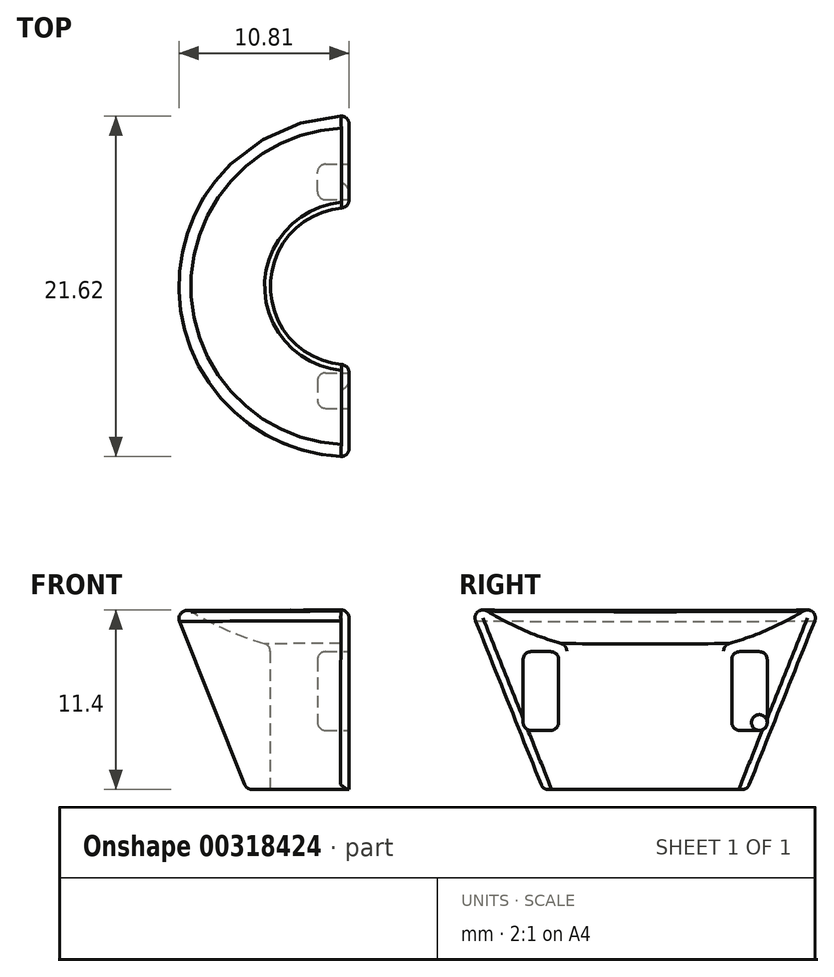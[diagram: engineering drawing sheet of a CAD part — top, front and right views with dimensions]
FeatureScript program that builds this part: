
annotation { "Feature Type Name" : "Feature", "Feature Type Description" : "" }
export const myFeature = defineFeature(function(context is Context, id is Id, definition is map)
    precondition{}
    {
        {
            var Q0;
            Q0=qCreatedBy(makeId("Top.planeOp"),FACE);
            var sketch = newSketch(context, id + "F0", { "sketchPlane" : qUnion([Q0])});
            skCircle(sketch, "E0", {"center": v(0, 0) * mm, "radius": 6.5 * mm});
            skSolve(sketch);
        }
        {
            var Q0;
            Q0=qCreatedBy(makeId("Top.planeOp"),FACE);
            cPlane(context, id + "F1", {"entities" : qUnion([Q0]), "cplaneType" : CPlaneType.OFFSET, "offset" : 15 * mm, "width" : 150 * mm, "height" : 150 * mm});
        }
        {
            var Q0;
            Q0=qCreatedBy(id+"F1.planeOp",FACE);
            var sketch = newSketch(context, id + "F2", { "sketchPlane" : qUnion([Q0])});
            skCircle(sketch, "E1", {"center": v(0, 0) * mm, "radius": 12.5 * mm});
            skSolve(sketch);
        }
        {
            var Q0;
            Q0=makeQuery(id+"F0.imprint","IMPRINT",FACE,{"disambiguationData":[TD([[makeQuery(id+"F0.imprint","IMPRINT",EDGE,{"derivedFrom":sQuery(id+"F0.wireOp",EDGE,"E0")}),1.0]])]});
            var Q1;
            Q1=makeQuery(id+"F2.imprint","IMPRINT",FACE,{"disambiguationData":[TD([[makeQuery(id+"F2.imprint","IMPRINT",EDGE,{"derivedFrom":sQuery(id+"F2.wireOp",EDGE,"E1")}),1.0]])]});
            loft(context, id + "F3", {"sheetProfilesArray" : [{ "sheetProfileEntities" : qUnion([Q0]) }, { "sheetProfileEntities" : qUnion([Q1]) }]});
        }
        {
            var Q0;
            Q0=makeQuery(id+"F3.opLoft","CAP_FACE",FACE,{"disambiguationData":[OSD([makeQuery(id+"F0.imprint","IMPRINT",FACE,{"disambiguationData":[TD([[makeQuery(id+"F0.imprint","IMPRINT",EDGE,{"derivedFrom":sQuery(id+"F0.wireOp",EDGE,"E0")}),1.0]])]})])],"isStart":true});
            var sketch = newSketch(context, id + "F4", { "sketchPlane" : qUnion([Q0])});
            skCircle(sketch, "E2", {"center": v(0, 0) * mm, "radius": 5 * mm});
            skSolve(sketch);
        }
        {
            var Q0;
            Q0=makeQuery(id+"F4.imprint","IMPRINT",FACE,{"disambiguationData":[TD([[makeQuery(id+"F4.imprint","IMPRINT",EDGE,{"derivedFrom":sQuery(id+"F4.wireOp",EDGE,"E2")}),1.0]])]});
            extrude(context, id + "F5", {"entities" : qUnion([Q0]), "operationType" : NewBodyOperationType.REMOVE, "oppositeDirection" : true, "depth" : 10 * mm});
        }
        {
            var Q0;
            Q0=qCreatedBy(makeId("Front.planeOp"),FACE);
            var sketch = newSketch(context, id + "F6", { "sketchPlane" : qUnion([Q0])});
            skArc(sketch, "E3", {"start": v(0.03, 47.5) * mm, "mid": v(-19.5, 28.09) * mm, "end": v(-0.14, 8.5) * mm});
            skLineSegment(sketch, "E4", {"start": v(-0.14, 8.5) * mm, "end": v(0.03, 47.5) * mm});
            skSolve(sketch);
        }
        {
            var Q0;
            Q0=makeQuery(id+"F6.imprint","IMPRINT",FACE,{"disambiguationData":[TD([[makeQuery(id+"F6.imprint","IMPRINT",EDGE,{"derivedFrom":sQuery(id+"F6.wireOp",EDGE,"E3")}),1.0]])]});
            var Q1;
            Q1=sQuery(id+"F6.wireOp",EDGE,"E4");
            revolve(context, id + "F7", {"operationType" : NewBodyOperationType.REMOVE, "entities" : qUnion([Q0]), "axis" : qUnion([Q1]), "revolveType" : RevolveType.FULL});
        }
        {
            var Q0;
            Q0=qCreatedBy(makeId("Front.planeOp"),FACE);
            var sketch = newSketch(context, id + "F8", { "sketchPlane" : qUnion([Q0])});
            skLineSegment(sketch, "E5.bottom", {"start": v(0, 0) * mm, "end": v(15, 0) * mm});
            skLineSegment(sketch, "E5.top", {"start": v(0, 15) * mm, "end": v(15, 15) * mm});
            skLineSegment(sketch, "E5.left", {"start": v(0, 0) * mm, "end": v(0, 15) * mm});
            skLineSegment(sketch, "E5.right", {"start": v(15, 0) * mm, "end": v(15, 15) * mm});
            skSolve(sketch);
        }
        {
            var Q0;
            Q0=makeQuery(id+"F8.imprint","IMPRINT",FACE,{"disambiguationData":[TD([[makeQuery(id+"F8.imprint","IMPRINT",EDGE,{"derivedFrom":sQuery(id+"F8.wireOp",EDGE,"E5.bottom")}),1.0]])]});
            extrude(context, id + "F9", {"entities" : qUnion([Q0]), "operationType" : NewBodyOperationType.REMOVE, "depth" : 25 * mm, "hasSecondDirection" : true, "secondDirectionOppositeDirection" : true, "secondDirectionDepth" : 25 * mm});
        }
        {
            var Q0;
            Q0=makeQuery(id+"FPjt2AgAj65mRvz_1.boolean.opBoolean","SPLIT",FACE,{"disambiguationData":[OD(0.0)],"derivedFrom":makeQuery(id+"F9.boolean.opBoolean","COPY",FACE,{"derivedFrom":makeQuery(id+"F9.opExtrude","SWEPT_FACE",FACE,{"disambiguationData":[OSD([sQuery(id+"F8.wireOp",EDGE,"E5.left")])]})})});
            var sketch = newSketch(context, id + "F10", { "sketchPlane" : qUnion([Q0])});
            skLineSegment(sketch, "E6.bottom", {"start": v(-6, 8.75) * mm, "end": v(-7.25, 8.75) * mm});
            skLineSegment(sketch, "E6.top", {"start": v(-6, 3.75) * mm, "end": v(-7.25, 3.75) * mm});
            skLineSegment(sketch, "E6.left", {"start": v(-5.5, 8.25) * mm, "end": v(-5.5, 4.25) * mm});
            skLineSegment(sketch, "E6.right", {"start": v(-7.75, 8.25) * mm, "end": v(-7.75, 4.25) * mm});
            skPoint(sketch, "E7.visualSharp", {"position": v(-7.75, 8.75) * mm});
            skArc(sketch, "E7.filletArc", {"start": v(-7.25, 8.75) * mm, "mid": v(-7.6, 8.6) * mm, "end": v(-7.75, 8.25) * mm});
            skPoint(sketch, "E8.visualSharp", {"position": v(-5.5, 8.75) * mm});
            skArc(sketch, "E8.filletArc", {"start": v(-5.5, 8.25) * mm, "mid": v(-5.65, 8.6) * mm, "end": v(-6, 8.75) * mm});
            skPoint(sketch, "E9.visualSharp", {"position": v(-5.5, 3.75) * mm});
            skArc(sketch, "E9.filletArc", {"start": v(-6, 3.75) * mm, "mid": v(-5.65, 3.9) * mm, "end": v(-5.5, 4.25) * mm});
            skPoint(sketch, "E10.visualSharp", {"position": v(-7.75, 3.75) * mm});
            skArc(sketch, "E10.filletArc", {"start": v(-7.75, 4.25) * mm, "mid": v(-7.6, 3.9) * mm, "end": v(-7.25, 3.75) * mm});
            skLineSegment(sketch, "E11.MirrorCS", {"start": v(5.5, 8.25) * mm, "end": v(5.5, 4.25) * mm});
            skArc(sketch, "E12.MirrorCS", {"start": v(5.5, 8.25) * mm, "mid": v(5.65, 8.6) * mm, "end": v(6, 8.75) * mm});
            skLineSegment(sketch, "E13.MirrorCS", {"start": v(6, 8.75) * mm, "end": v(7.25, 8.75) * mm});
            skArc(sketch, "E14.MirrorCS", {"start": v(7.25, 8.75) * mm, "mid": v(7.6, 8.6) * mm, "end": v(7.75, 8.25) * mm});
            skLineSegment(sketch, "E15.MirrorCS", {"start": v(7.75, 8.25) * mm, "end": v(7.75, 4.25) * mm});
            skPoint(sketch, "E16.MirrorP", {"position": v(7.75, 3.75) * mm});
            skArc(sketch, "E17.MirrorCS", {"start": v(7.75, 4.25) * mm, "mid": v(7.6, 3.9) * mm, "end": v(7.25, 3.75) * mm});
            skLineSegment(sketch, "E18.MirrorCS", {"start": v(6, 3.75) * mm, "end": v(7.25, 3.75) * mm});
            skArc(sketch, "E19.MirrorCS", {"start": v(6, 3.75) * mm, "mid": v(5.65, 3.9) * mm, "end": v(5.5, 4.25) * mm});
            skSolve(sketch);
        }
        {
            var Q0;
            Q0=makeQuery(id+"F10.imprint","IMPRINT",FACE,{"disambiguationData":[TD([[makeQuery(id+"F10.imprint","IMPRINT",EDGE,{"derivedFrom":sQuery(id+"F10.wireOp",EDGE,"E6.bottom")}),1.0]])]});
            var Q1;
            Q1=makeQuery(id+"F10.imprint","IMPRINT",FACE,{"disambiguationData":[TD([[makeQuery(id+"F10.imprint","IMPRINT",EDGE,{"derivedFrom":sQuery(id+"F10.wireOp",EDGE,"E11.MirrorCS")}),1.0]])]});
            extrude(context, id + "F11", {"entities" : qUnion([Q0, Q1]), "operationType" : NewBodyOperationType.REMOVE, "oppositeDirection" : true, "depth" : 2 * mm});
        }
        {
            var Q0;
            Q0=makeQuery(id+"F7.boolean.opBoolean","INTERSECT",EDGE,{"derivedFrom":[makeQuery(id+"F3.opLoft","SWEPT_FACE",FACE,{"disambiguationData":[OSD([sQuery(id+"F0.wireOp",EDGE,"E0"),sQuery(id+"F2.wireOp",EDGE,"E1")])]}),makeQuery(id+"F7.opRevolve","SWEPT_FACE",FACE,{"disambiguationData":[OSD([sQuery(id+"F6.wireOp",EDGE,"E3")])]})]});
            var Q1;
            Q1=makeQuery(id+"F3.opLoft","MID_CAP_EDGE",EDGE,{"disambiguationData":[OSD([sQuery(id+"F0.wireOp",EDGE,"E0")])],"capPos":0.0});
            var Q2;
            Q2=makeQuery(id+"F5.boolean.opBoolean","COPY",EDGE,{"derivedFrom":makeQuery(id+"F5.opExtrude","CAP_EDGE",EDGE,{"disambiguationData":[OSD([sQuery(id+"F4.wireOp",EDGE,"E2")])],"isStart":true})});
            var Q3;
            Q3=makeQuery(id+"F9.boolean.opBoolean","INTERSECT",EDGE,{"disambiguationData":[OD(0.0)],"derivedFrom":[makeQuery(id+"F5.boolean.opBoolean","COPY",FACE,{"derivedFrom":makeQuery(id+"F5.opExtrude","SWEPT_FACE",FACE,{"disambiguationData":[OSD([sQuery(id+"F4.wireOp",EDGE,"E2")])]})}),makeQuery(id+"F9.opExtrude","SWEPT_FACE",FACE,{"disambiguationData":[OSD([sQuery(id+"F8.wireOp",EDGE,"E5.left")])]})]});
            var Q4;
            Q4=makeQuery(id+"F9.boolean.opBoolean","INTERSECT",EDGE,{"disambiguationData":[OD(1.0)],"derivedFrom":[makeQuery(id+"F5.boolean.opBoolean","COPY",FACE,{"derivedFrom":makeQuery(id+"F5.opExtrude","SWEPT_FACE",FACE,{"disambiguationData":[OSD([sQuery(id+"F4.wireOp",EDGE,"E2")])]})}),makeQuery(id+"F9.opExtrude","SWEPT_FACE",FACE,{"disambiguationData":[OSD([sQuery(id+"F8.wireOp",EDGE,"E5.left")])]})]});
            var Q5;
            Q5=makeQuery(id+"F7.boolean.opBoolean","INTERSECT",EDGE,{"derivedFrom":[makeQuery(id+"F5.boolean.opBoolean","COPY",FACE,{"derivedFrom":makeQuery(id+"F5.opExtrude","SWEPT_FACE",FACE,{"disambiguationData":[OSD([sQuery(id+"F4.wireOp",EDGE,"E2")])]})}),makeQuery(id+"F7.opRevolve","SWEPT_FACE",FACE,{"disambiguationData":[OSD([sQuery(id+"F6.wireOp",EDGE,"E3")])]})]});
            var Q6;
            Q6=makeQuery(id+"F9.boolean.opBoolean","INTERSECT",EDGE,{"disambiguationData":[OD(1.0)],"derivedFrom":[makeQuery(id+"F7.boolean.opBoolean","COPY",FACE,{"derivedFrom":makeQuery(id+"F7.opRevolve","SWEPT_FACE",FACE,{"disambiguationData":[OSD([sQuery(id+"F6.wireOp",EDGE,"E3")])]})}),makeQuery(id+"F9.opExtrude","SWEPT_FACE",FACE,{"disambiguationData":[OSD([sQuery(id+"F8.wireOp",EDGE,"E5.left")])]})]});
            var Q7;
            Q7=makeQuery(id+"F9.boolean.opBoolean","INTERSECT",EDGE,{"disambiguationData":[OD(0.0)],"derivedFrom":[makeQuery(id+"F7.boolean.opBoolean","COPY",FACE,{"derivedFrom":makeQuery(id+"F7.opRevolve","SWEPT_FACE",FACE,{"disambiguationData":[OSD([sQuery(id+"F6.wireOp",EDGE,"E3")])]})}),makeQuery(id+"F9.opExtrude","SWEPT_FACE",FACE,{"disambiguationData":[OSD([sQuery(id+"F8.wireOp",EDGE,"E5.left")])]})]});
            var Q8;
            Q8=makeQuery(id+"F11.opExtrude","CAP_EDGE",EDGE,{"disambiguationData":[OSD([sQuery(id+"F10.wireOp",EDGE,"E6.right")])],"isStart":false});
            var Q9;
            Q9=makeQuery(id+"F11.opExtrude","CAP_EDGE",EDGE,{"disambiguationData":[OSD([sQuery(id+"F10.wireOp",EDGE,"E6.left")])],"isStart":false});
            var Q10;
            Q10=makeQuery(id+"F11.opExtrude","CAP_EDGE",EDGE,{"disambiguationData":[OSD([sQuery(id+"F10.wireOp",EDGE,"E11.MirrorCS")])],"isStart":false});
            var Q11;
            Q11=makeQuery(id+"F11.boolean.opBoolean","COPY",EDGE,{"derivedFrom":makeQuery(id+"F11.opExtrude","CAP_EDGE",EDGE,{"disambiguationData":[OSD([sQuery(id+"F10.wireOp",EDGE,"E6.left")])],"isStart":false})});
            var Q12;
            Q12=makeQuery(id+"F11.boolean.opBoolean","COPY",EDGE,{"derivedFrom":makeQuery(id+"F11.opExtrude","CAP_EDGE",EDGE,{"disambiguationData":[OSD([sQuery(id+"F10.wireOp",EDGE,"E15.MirrorCS")])],"isStart":false})});
            var Q13;
            Q13=makeQuery(id+"F9.boolean.opBoolean","INTERSECT",EDGE,{"disambiguationData":[OD(0.0)],"derivedFrom":[makeQuery(id+"F3.opLoft","SWEPT_FACE",FACE,{"disambiguationData":[OSD([sQuery(id+"F0.wireOp",EDGE,"E0"),sQuery(id+"F2.wireOp",EDGE,"E1")])]}),makeQuery(id+"F9.opExtrude","SWEPT_FACE",FACE,{"disambiguationData":[OSD([sQuery(id+"F8.wireOp",EDGE,"E5.left")])]})]});
            var Q14;
            Q14=makeQuery(id+"F9.boolean.opBoolean","INTERSECT",EDGE,{"disambiguationData":[OD(1.0)],"derivedFrom":[makeQuery(id+"F3.opLoft","SWEPT_FACE",FACE,{"disambiguationData":[OSD([sQuery(id+"F0.wireOp",EDGE,"E0"),sQuery(id+"F2.wireOp",EDGE,"E1")])]}),makeQuery(id+"F9.opExtrude","SWEPT_FACE",FACE,{"disambiguationData":[OSD([sQuery(id+"F8.wireOp",EDGE,"E5.left")])]})]});
            fillet(context, id + "F12", {"entities" : qUnion([Q0, Q1, Q2, Q3, Q4, Q5, Q6, Q7, Q8, Q9, Q10, Q11, Q12, Q13, Q14]), "radius" : .5 * mm, "tangentPropagation" : true, "allowEdgeOverflow" : false});
        }
    });
